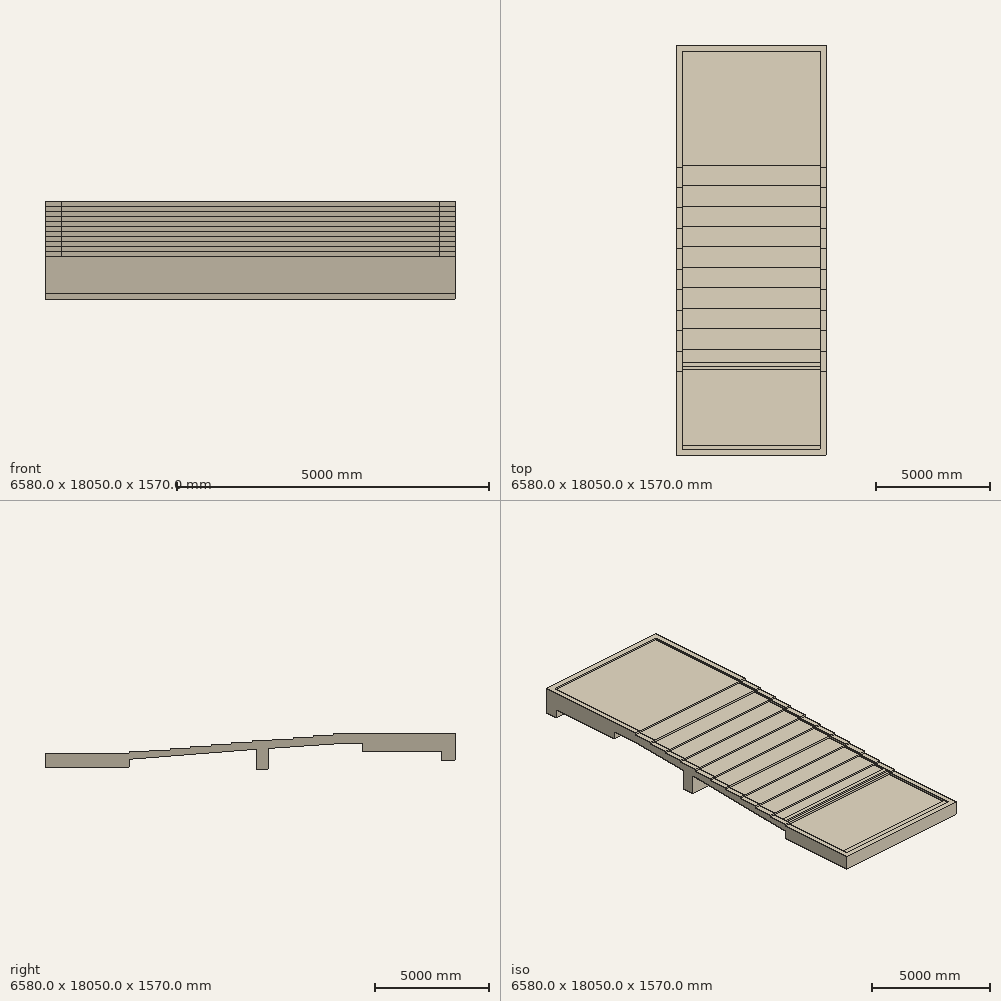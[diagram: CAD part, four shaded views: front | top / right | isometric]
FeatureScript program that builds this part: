
annotation { "Feature Type Name" : "Feature", "Feature Type Description" : "" }
export const myFeature = defineFeature(function(context is Context, id is Id, definition is map)
    precondition{}
    {
        {
            var Q0;
            Q0=qCreatedBy(makeId("Right.planeOp"),FACE);
            var sketch = newSketch(context, id + "F0", { "sketchPlane" : qUnion([Q0])});
            skLineSegment(sketch, "E0", {"start": v(0, 0) * mm, "end": v(-900, 0) * mm});
            skLineSegment(sketch, "E1", {"start": v(-900, 0) * mm, "end": v(-900, -80) * mm});
            skLineSegment(sketch, "E2", {"start": v(-900, -80) * mm, "end": v(-1800, -80) * mm});
            skLineSegment(sketch, "E3", {"start": v(-1800, -80) * mm, "end": v(-1800, -160) * mm});
            skLineSegment(sketch, "E4", {"start": v(-1800, -160) * mm, "end": v(-2700, -160) * mm});
            skLineSegment(sketch, "E5", {"start": v(-2700, -160) * mm, "end": v(-2700, -240) * mm});
            skLineSegment(sketch, "E6", {"start": v(-2700, -240) * mm, "end": v(-3600, -240) * mm});
            skLineSegment(sketch, "E7", {"start": v(-3600, -240) * mm, "end": v(-3600, -320) * mm});
            skLineSegment(sketch, "E8", {"start": v(-3600, -320) * mm, "end": v(-4500, -320) * mm});
            skLineSegment(sketch, "E9", {"start": v(-4500, -320) * mm, "end": v(-4500, -400) * mm});
            skLineSegment(sketch, "E10", {"start": v(-4500, -400) * mm, "end": v(-5400, -400) * mm});
            skLineSegment(sketch, "E11", {"start": v(-5400, -400) * mm, "end": v(-5400, -480) * mm});
            skLineSegment(sketch, "E12", {"start": v(-5400, -480) * mm, "end": v(-6300, -480) * mm});
            skLineSegment(sketch, "E13", {"start": v(-6300, -480) * mm, "end": v(-6300, -560) * mm});
            skLineSegment(sketch, "E14", {"start": v(-6300, -560) * mm, "end": v(-7200, -560) * mm});
            skLineSegment(sketch, "E15", {"start": v(-7200, -560) * mm, "end": v(-7200, -640) * mm});
            skLineSegment(sketch, "E16", {"start": v(-7200, -640) * mm, "end": v(-8100, -640) * mm});
            skLineSegment(sketch, "E17", {"start": v(-8100, -640) * mm, "end": v(-8100, -720) * mm});
            skLineSegment(sketch, "E18", {"start": v(-8100, -720) * mm, "end": v(-9000, -720) * mm});
            skLineSegment(sketch, "E19", {"start": v(-9000, -720) * mm, "end": v(-9000, -800) * mm});
            skLineSegment(sketch, "E20", {"start": v(-9000, -800) * mm, "end": v(-12450, -800) * mm});
            skLineSegment(sketch, "E21", {"start": v(-12450, -800) * mm, "end": v(-12700, -800) * mm});
            skLineSegment(sketch, "E22", {"start": v(-12700, -800) * mm, "end": v(-12700, -800) * mm});
            skLineSegment(sketch, "E23", {"start": v(-12700, -800) * mm, "end": v(-12700, -1300) * mm});
            skLineSegment(sketch, "E24", {"start": v(-12700, -1300) * mm, "end": v(-12700, -1400) * mm});
            skLineSegment(sketch, "E25", {"start": v(-12700, -1400) * mm, "end": v(-9000, -1400) * mm});
            skLineSegment(sketch, "E26", {"start": v(0, 0) * mm, "end": v(0, 80) * mm});
            skLineSegment(sketch, "E27", {"start": v(0, 80) * mm, "end": v(5250, 80) * mm});
            skLineSegment(sketch, "E28", {"start": v(5250, 80) * mm, "end": v(5350, 80) * mm});
            skLineSegment(sketch, "E29", {"start": v(5350, 80) * mm, "end": v(5350, -20) * mm});
            skLineSegment(sketch, "E30", {"start": v(5350, -20) * mm, "end": v(5350, -1020) * mm});
            skLineSegment(sketch, "E31", {"start": v(5350, -1020) * mm, "end": v(5350, -1120) * mm});
            skLineSegment(sketch, "E32", {"start": v(5350, -1120) * mm, "end": v(4750, -1120) * mm});
            skLineSegment(sketch, "E33", {"start": v(4750, -1120) * mm, "end": v(4750, -720) * mm});
            skLineSegment(sketch, "E34", {"start": v(4750, -720) * mm, "end": v(1250, -720) * mm});
            skLineSegment(sketch, "E35", {"start": v(1250, -720) * mm, "end": v(1250, -370) * mm});
            skLineSegment(sketch, "E36", {"start": v(80, 0) * mm, "end": v(80, -80) * mm});
            skLineSegment(sketch, "E37", {"start": v(80, -80) * mm, "end": v(-820, -80) * mm});
            skLineSegment(sketch, "E38", {"start": v(-820, -80) * mm, "end": v(-820, -160) * mm});
            skLineSegment(sketch, "E39", {"start": v(-820, -160) * mm, "end": v(-1720, -160) * mm});
            skLineSegment(sketch, "E40", {"start": v(-1720, -160) * mm, "end": v(-1720, -240) * mm});
            skLineSegment(sketch, "E41", {"start": v(-1720, -240) * mm, "end": v(-2620, -240) * mm});
            skLineSegment(sketch, "E42", {"start": v(-2620, -240) * mm, "end": v(-2620, -320) * mm});
            skLineSegment(sketch, "E43", {"start": v(-2620, -320) * mm, "end": v(-3520, -320) * mm});
            skLineSegment(sketch, "E44", {"start": v(-3520, -320) * mm, "end": v(-3520, -400) * mm});
            skLineSegment(sketch, "E45", {"start": v(-3520, -400) * mm, "end": v(-4420, -400) * mm});
            skLineSegment(sketch, "E46", {"start": v(-4420, -400) * mm, "end": v(-4420, -480) * mm});
            skLineSegment(sketch, "E47", {"start": v(-4420, -480) * mm, "end": v(-5320, -480) * mm});
            skLineSegment(sketch, "E48", {"start": v(-5320, -480) * mm, "end": v(-5320, -560) * mm});
            skLineSegment(sketch, "E49", {"start": v(-5320, -560) * mm, "end": v(-6220, -560) * mm});
            skLineSegment(sketch, "E50", {"start": v(-6220, -560) * mm, "end": v(-6220, -640) * mm});
            skLineSegment(sketch, "E51", {"start": v(-6220, -640) * mm, "end": v(-7120, -640) * mm});
            skLineSegment(sketch, "E52", {"start": v(-7120, -640) * mm, "end": v(-7120, -720) * mm});
            skLineSegment(sketch, "E53", {"start": v(-7120, -720) * mm, "end": v(-8020, -720) * mm});
            skLineSegment(sketch, "E54", {"start": v(-8020, -720) * mm, "end": v(-8020, -800) * mm});
            skLineSegment(sketch, "E55", {"start": v(-8020, -800) * mm, "end": v(-8920, -800) * mm});
            skLineSegment(sketch, "E56", {"start": v(-8920, -800) * mm, "end": v(-8920, -880) * mm});
            skLineSegment(sketch, "E57", {"start": v(-8920, -880) * mm, "end": v(-12450, -880) * mm});
            skLineSegment(sketch, "E58", {"start": v(-12450, -880) * mm, "end": v(-12450, -800) * mm});
            skLineSegment(sketch, "E59.0", {"start": v(-12300, -880) * mm, "end": v(-12300, -800) * mm});
            skLineSegment(sketch, "E60", {"start": v(5250, 80) * mm, "end": v(5100, 80) * mm});
            skLineSegment(sketch, "E61", {"start": v(5100, 80) * mm, "end": v(5100, 0) * mm});
            skLineSegment(sketch, "E62", {"start": v(5100, 0) * mm, "end": v(80, 0) * mm});
            skLineSegment(sketch, "E63", {"start": v(1250, -370) * mm, "end": v(80, -370) * mm});
            skLineSegment(sketch, "E64", {"start": v(-3150, -240) * mm, "end": v(-3150, -320) * mm});
            skLineSegment(sketch, "E65", {"start": v(-3150, -590) * mm, "end": v(-3150, -1390) * mm});
            skLineSegment(sketch, "E66", {"start": v(-3150, -1390) * mm, "end": v(-3150, -1490) * mm});
            skPoint(sketch, "E66.endSnap0", {"position": v(-3150, -990) * mm});
            skLineSegment(sketch, "E67", {"start": v(80, -370) * mm, "end": v(-2875, -571.27) * mm});
            skLineSegment(sketch, "E68", {"start": v(-3150, -1490) * mm, "end": v(-2875, -1490) * mm});
            skLineSegment(sketch, "E69", {"start": v(-2875, -1490) * mm, "end": v(-2875, -571.27) * mm});
            skLineSegment(sketch, "E70.MirrorCS", {"start": v(-3425, -1490) * mm, "end": v(-3425, -571.27) * mm});
            skLineSegment(sketch, "E71", {"start": v(-3150, -1490) * mm, "end": v(-3425, -1490) * mm});
            skLineSegment(sketch, "E72", {"start": v(-9000, -1400) * mm, "end": v(-9000, -1050) * mm});
            skLineSegment(sketch, "E73", {"start": v(-9000, -1050) * mm, "end": v(-3425, -608.73) * mm});
            skSolve(sketch);
        }
        {
            var Q0;
            Q0=makeQuery(id+"F0.imprint","IMPRINT",FACE,{"disambiguationData":[TD([[makeQuery(id+"F0.imprint","IMPRINT",EDGE,{"derivedFrom":sQuery(id+"F0.wireOp",EDGE,"E21")}),1.0]])]});
            extrude(context, id + "F1", {"entities" : qUnion([Q0]), "depth" : 6280 * mm, "offsetDistance" : 25 * mm, "symmetric" : true});
        }
        {
            var Q0;
            {var subQ6=sQuery(id+"F0.wireOp",EDGE,"E7");Q0=makeQuery(id+"F0.imprint","IMPRINT",FACE,{"disambiguationData":[TD([[makeQuery(id+"F0.imprint","IMPRINT",EDGE,{"derivedFrom":subQ6}),1.0]])]});}
            var Q1;
            {var subQ7=sQuery(id+"F0.wireOp",EDGE,"E0");Q1=makeQuery(id+"F0.imprint","IMPRINT",FACE,{"disambiguationData":[TD([[makeQuery(id+"F0.imprint","IMPRINT",EDGE,{"derivedFrom":subQ7}),1.0]])]});}
            var Q2;
            {var subQ0=sQuery(id+"F0.wireOp",EDGE,"E58");Q2=makeQuery(id+"F0.imprint","IMPRINT",FACE,{"disambiguationData":[TD([[makeQuery(id+"F0.imprint","IMPRINT",EDGE,{"derivedFrom":subQ0}),-1.0]])]});}
            var Q3;
            Q3=makeQuery(id+"F0.imprint","IMPRINT",FACE,{"disambiguationData":[TD([[makeQuery(id+"F0.imprint","IMPRINT",EDGE,{"derivedFrom":sQuery(id+"F0.wireOp",EDGE,"E21")}),1.0]])]});
            extrude(context, id + "F2", {"entities" : qUnion([Q0, Q1, Q2, Q3]), "operationType" : NewBodyOperationType.ADD, "depth" : 3290 * mm, "offsetDistance" : 25 * mm, "hasSecondDirection" : true, "secondDirectionOppositeDirection" : false, "secondDirectionDepth" : 3040 * mm});
        }
        {
            var Q0;
            Q0=makeQuery(id+"F0.imprint","IMPRINT",FACE,{"disambiguationData":[TD([[makeQuery(id+"F0.imprint","IMPRINT",EDGE,{"derivedFrom":sQuery(id+"F0.wireOp",EDGE,"E21")}),1.0]])]});
            var Q1;
            Q1=makeQuery(id+"F0.imprint","IMPRINT",FACE,{"disambiguationData":[TD([[makeQuery(id+"F0.imprint","IMPRINT",EDGE,{"derivedFrom":sQuery(id+"F0.wireOp",EDGE,"E0")}),1.0]])]});
            var Q2;
            {var subQ6=sQuery(id+"F0.wireOp",EDGE,"E7");Q2=makeQuery(id+"F0.imprint","IMPRINT",FACE,{"disambiguationData":[TD([[makeQuery(id+"F0.imprint","IMPRINT",EDGE,{"derivedFrom":subQ6}),1.0]])]});}
            var Q3;
            {var subQ0=sQuery(id+"F0.wireOp",EDGE,"E58");Q3=makeQuery(id+"F0.imprint","IMPRINT",FACE,{"disambiguationData":[TD([[makeQuery(id+"F0.imprint","IMPRINT",EDGE,{"derivedFrom":subQ0}),-1.0]])]});}
            extrude(context, id + "F3", {"entities" : qUnion([Q0, Q1, Q2, Q3]), "operationType" : NewBodyOperationType.ADD, "oppositeDirection" : true, "depth" : 3290 * mm, "offsetDistance" : 25 * mm, "hasSecondDirection" : true, "secondDirectionOppositeDirection" : true, "secondDirectionDepth" : 3040 * mm});
        }
        {
            var Q0;
            Q0=qCreatedBy(makeId("Right.planeOp"),FACE);
            var sketch = newSketch(context, id + "F4", { "sketchPlane" : qUnion([Q0])});
            skLineSegment(sketch, "E74", {"start": v(0, 0) * mm, "end": v(-900, 0) * mm});
            skLineSegment(sketch, "E75", {"start": v(-900, 0) * mm, "end": v(-900, -80) * mm});
            skLineSegment(sketch, "E76", {"start": v(-900, -80) * mm, "end": v(-1800, -80) * mm});
            skLineSegment(sketch, "E77", {"start": v(-1800, -80) * mm, "end": v(-1800, -160) * mm});
            skLineSegment(sketch, "E78", {"start": v(-1800, -160) * mm, "end": v(-2700, -160) * mm});
            skLineSegment(sketch, "E79", {"start": v(-2700, -160) * mm, "end": v(-2700, -240) * mm});
            skLineSegment(sketch, "E80", {"start": v(-2700, -240) * mm, "end": v(-3600, -240) * mm});
            skLineSegment(sketch, "E81", {"start": v(-3600, -240) * mm, "end": v(-3600, -320) * mm});
            skLineSegment(sketch, "E82", {"start": v(-3600, -320) * mm, "end": v(-4500, -320) * mm});
            skLineSegment(sketch, "E83", {"start": v(-4500, -320) * mm, "end": v(-4500, -400) * mm});
            skLineSegment(sketch, "E84", {"start": v(-4500, -400) * mm, "end": v(-5400, -400) * mm});
            skLineSegment(sketch, "E85", {"start": v(-5400, -400) * mm, "end": v(-5400, -480) * mm});
            skLineSegment(sketch, "E86", {"start": v(-5400, -480) * mm, "end": v(-6300, -480) * mm});
            skLineSegment(sketch, "E87", {"start": v(-6300, -480) * mm, "end": v(-6300, -560) * mm});
            skLineSegment(sketch, "E88", {"start": v(-6300, -560) * mm, "end": v(-7200, -560) * mm});
            skLineSegment(sketch, "E89", {"start": v(-7200, -560) * mm, "end": v(-7200, -640) * mm});
            skLineSegment(sketch, "E90", {"start": v(-7200, -640) * mm, "end": v(-8100, -640) * mm});
            skLineSegment(sketch, "E91", {"start": v(-8100, -640) * mm, "end": v(-8100, -720) * mm});
            skLineSegment(sketch, "E92", {"start": v(-8100, -720) * mm, "end": v(-9000, -720) * mm});
            skLineSegment(sketch, "E93", {"start": v(-9000, -720) * mm, "end": v(-9000, -800) * mm});
            skLineSegment(sketch, "E94", {"start": v(-9000, -800) * mm, "end": v(-12450, -800) * mm});
            skLineSegment(sketch, "E95", {"start": v(-12450, -800) * mm, "end": v(-12450, -880) * mm});
            skLineSegment(sketch, "E96", {"start": v(-12450, -880) * mm, "end": v(-8920, -880) * mm});
            skLineSegment(sketch, "E97", {"start": v(-8920, -880) * mm, "end": v(-8920, -800) * mm});
            skLineSegment(sketch, "E98", {"start": v(-8920, -800) * mm, "end": v(-8020, -800) * mm});
            skLineSegment(sketch, "E99", {"start": v(-8020, -800) * mm, "end": v(-8020, -720) * mm});
            skLineSegment(sketch, "E100", {"start": v(-8020, -720) * mm, "end": v(-7120, -720) * mm});
            skLineSegment(sketch, "E101", {"start": v(-7120, -720) * mm, "end": v(-7120, -640.41) * mm});
            skLineSegment(sketch, "E102", {"start": v(-7120, -640.41) * mm, "end": v(-6220, -640.41) * mm});
            skLineSegment(sketch, "E103", {"start": v(-6220, -640.41) * mm, "end": v(-6220, -560.41) * mm});
            skLineSegment(sketch, "E104", {"start": v(-6220, -560.41) * mm, "end": v(-5320, -560.41) * mm});
            skLineSegment(sketch, "E105", {"start": v(-5320, -560.41) * mm, "end": v(-5320, -480.41) * mm});
            skLineSegment(sketch, "E106", {"start": v(-5320, -480.41) * mm, "end": v(-4420, -480.41) * mm});
            skLineSegment(sketch, "E107", {"start": v(-4420, -480.41) * mm, "end": v(-4420, -400.41) * mm});
            skLineSegment(sketch, "E108", {"start": v(-4420, -400.41) * mm, "end": v(-3520, -400.41) * mm});
            skLineSegment(sketch, "E109", {"start": v(-3520, -400.41) * mm, "end": v(-3520, -320.41) * mm});
            skLineSegment(sketch, "E110", {"start": v(-3520, -320.41) * mm, "end": v(-2620, -320.41) * mm});
            skLineSegment(sketch, "E111", {"start": v(-2620, -320.41) * mm, "end": v(-2620, -240.41) * mm});
            skLineSegment(sketch, "E112", {"start": v(-2620, -240.41) * mm, "end": v(-1720, -240.41) * mm});
            skLineSegment(sketch, "E113", {"start": v(-1720, -240.41) * mm, "end": v(-1720, -160.41) * mm});
            skLineSegment(sketch, "E114", {"start": v(-1720, -160.41) * mm, "end": v(-820, -160.41) * mm});
            skLineSegment(sketch, "E115", {"start": v(-820, -160.41) * mm, "end": v(-820, -80.41) * mm});
            skLineSegment(sketch, "E116", {"start": v(-820, -80.41) * mm, "end": v(80, -80.41) * mm});
            skLineSegment(sketch, "E117", {"start": v(0, 0) * mm, "end": v(0, 80) * mm});
            skLineSegment(sketch, "E118", {"start": v(0, 80) * mm, "end": v(5250, 80) * mm});
            skLineSegment(sketch, "E119", {"start": v(5250, 80) * mm, "end": v(5100, 80) * mm});
            skLineSegment(sketch, "E120", {"start": v(5100, 80) * mm, "end": v(5100, 0) * mm});
            skLineSegment(sketch, "E121", {"start": v(5100, 0) * mm, "end": v(80, 0) * mm});
            skLineSegment(sketch, "E122", {"start": v(80, 0) * mm, "end": v(80, -80.41) * mm});
            skLineSegment(sketch, "E123", {"start": v(-9000, -800) * mm, "end": v(-8920, -800) * mm});
            skLineSegment(sketch, "E124", {"start": v(-12450, -800) * mm, "end": v(-12253.89, -800) * mm});
            skLineSegment(sketch, "E125", {"start": v(-12253.89, -800) * mm, "end": v(-12253.89, -880) * mm});
            skLineSegment(sketch, "E126.0", {"start": v(-12254.89, -800) * mm, "end": v(-12254.89, -880) * mm});
            skLineSegment(sketch, "E127.0", {"start": v(-12252.89, -800) * mm, "end": v(-12252.89, -880) * mm});
            skLineSegment(sketch, "E128.1.0.0", {"start": v(-12058.78, -800) * mm, "end": v(-12058.78, -880) * mm});
            skLineSegment(sketch, "E128.1.0.1", {"start": v(-12056.78, -800) * mm, "end": v(-12056.78, -880) * mm});
            skLineSegment(sketch, "E128.2.0.0", {"start": v(-11862.67, -800) * mm, "end": v(-11862.67, -880) * mm});
            skLineSegment(sketch, "E128.2.0.1", {"start": v(-11860.67, -800) * mm, "end": v(-11860.67, -880) * mm});
            skLineSegment(sketch, "E128.3.0.0", {"start": v(-11666.56, -800) * mm, "end": v(-11666.56, -880) * mm});
            skLineSegment(sketch, "E128.3.0.1", {"start": v(-11664.56, -800) * mm, "end": v(-11664.56, -880) * mm});
            skLineSegment(sketch, "E128.4.0.0", {"start": v(-11470.44, -800) * mm, "end": v(-11470.44, -880) * mm});
            skLineSegment(sketch, "E128.4.0.1", {"start": v(-11468.44, -800) * mm, "end": v(-11468.44, -880) * mm});
            skLineSegment(sketch, "E128.5.0.0", {"start": v(-11274.33, -800) * mm, "end": v(-11274.33, -880) * mm});
            skLineSegment(sketch, "E128.5.0.1", {"start": v(-11272.33, -800) * mm, "end": v(-11272.33, -880) * mm});
            skLineSegment(sketch, "E128.6.0.0", {"start": v(-11078.22, -800) * mm, "end": v(-11078.22, -880) * mm});
            skLineSegment(sketch, "E128.6.0.1", {"start": v(-11076.22, -800) * mm, "end": v(-11076.22, -880) * mm});
            skLineSegment(sketch, "E128.7.0.0", {"start": v(-10882.11, -800) * mm, "end": v(-10882.11, -880) * mm});
            skLineSegment(sketch, "E128.7.0.1", {"start": v(-10880.11, -800) * mm, "end": v(-10880.11, -880) * mm});
            skLineSegment(sketch, "E128.8.0.0", {"start": v(-10686, -800) * mm, "end": v(-10686, -880) * mm});
            skLineSegment(sketch, "E128.8.0.1", {"start": v(-10684, -800) * mm, "end": v(-10684, -880) * mm});
            skLineSegment(sketch, "E128.9.0.0", {"start": v(-10489.89, -800) * mm, "end": v(-10489.89, -880) * mm});
            skLineSegment(sketch, "E128.9.0.1", {"start": v(-10487.89, -800) * mm, "end": v(-10487.89, -880) * mm});
            skLineSegment(sketch, "E128.10.0.0", {"start": v(-10293.78, -800) * mm, "end": v(-10293.78, -880) * mm});
            skLineSegment(sketch, "E128.10.0.1", {"start": v(-10291.78, -800) * mm, "end": v(-10291.78, -880) * mm});
            skLineSegment(sketch, "E128.11.0.0", {"start": v(-10097.67, -800) * mm, "end": v(-10097.67, -880) * mm});
            skLineSegment(sketch, "E128.11.0.1", {"start": v(-10095.67, -800) * mm, "end": v(-10095.67, -880) * mm});
            skLineSegment(sketch, "E128.12.0.0", {"start": v(-9901.56, -800) * mm, "end": v(-9901.56, -880) * mm});
            skLineSegment(sketch, "E128.12.0.1", {"start": v(-9899.56, -800) * mm, "end": v(-9899.56, -880) * mm});
            skLineSegment(sketch, "E128.13.0.0", {"start": v(-9705.44, -800) * mm, "end": v(-9705.44, -880) * mm});
            skLineSegment(sketch, "E128.13.0.1", {"start": v(-9703.44, -800) * mm, "end": v(-9703.44, -880) * mm});
            skLineSegment(sketch, "E128.14.0.0", {"start": v(-9509.33, -800) * mm, "end": v(-9509.33, -880) * mm});
            skLineSegment(sketch, "E128.14.0.1", {"start": v(-9507.33, -800) * mm, "end": v(-9507.33, -880) * mm});
            skLineSegment(sketch, "E128.15.0.0", {"start": v(-9313.22, -800) * mm, "end": v(-9313.22, -880) * mm});
            skLineSegment(sketch, "E128.15.0.1", {"start": v(-9311.22, -800) * mm, "end": v(-9311.22, -880) * mm});
            skLineSegment(sketch, "E128.16.0.0", {"start": v(-9117.11, -800) * mm, "end": v(-9117.11, -880) * mm});
            skLineSegment(sketch, "E128.16.0.1", {"start": v(-9115.11, -800) * mm, "end": v(-9115.11, -880) * mm});
            skLineSegment(sketch, "E128.direction1", {"start": v(-12254.89, -880) * mm, "end": v(-12058.78, -880) * mm, "construction": true});
            skLineSegment(sketch, "E129", {"start": v(-9000, -720) * mm, "end": v(-8804, -720) * mm});
            skLineSegment(sketch, "E130", {"start": v(-8804, -720) * mm, "end": v(-8805, -720) * mm});
            skLineSegment(sketch, "E131", {"start": v(-8805, -720) * mm, "end": v(-8805, -800) * mm});
            skLineSegment(sketch, "E132", {"start": v(-8804, -720) * mm, "end": v(-8803, -720) * mm});
            skLineSegment(sketch, "E133", {"start": v(-8803, -720) * mm, "end": v(-8803, -800) * mm});
            skLineSegment(sketch, "E134.1.0.0", {"start": v(-8609, -720) * mm, "end": v(-8609, -800) * mm});
            skLineSegment(sketch, "E134.1.0.1", {"start": v(-8607, -720) * mm, "end": v(-8607, -800) * mm});
            skLineSegment(sketch, "E134.2.0.0", {"start": v(-8413, -720) * mm, "end": v(-8413, -800) * mm});
            skLineSegment(sketch, "E134.2.0.1", {"start": v(-8411, -720) * mm, "end": v(-8411, -800) * mm});
            skLineSegment(sketch, "E134.3.0.0", {"start": v(-8217, -720) * mm, "end": v(-8217, -800) * mm});
            skLineSegment(sketch, "E134.3.0.1", {"start": v(-8215, -720) * mm, "end": v(-8215, -800) * mm});
            skLineSegment(sketch, "E134.direction1", {"start": v(-8805, -800) * mm, "end": v(-8609, -800) * mm, "construction": true});
            skLineSegment(sketch, "E135", {"start": v(-8100, -720) * mm, "end": v(-8020, -720) * mm});
            skLineSegment(sketch, "E136", {"start": v(-8100, -640) * mm, "end": v(-7904, -640) * mm});
            skLineSegment(sketch, "E137", {"start": v(-7904, -640) * mm, "end": v(-7905, -640) * mm});
            skLineSegment(sketch, "E138", {"start": v(-7905, -640) * mm, "end": v(-7903, -640) * mm});
            skLineSegment(sketch, "E139", {"start": v(-7903, -640) * mm, "end": v(-7903, -720) * mm});
            skLineSegment(sketch, "E140", {"start": v(-7905, -640) * mm, "end": v(-7905, -720) * mm});
            skLineSegment(sketch, "E141.1.0.0", {"start": v(-7709, -640) * mm, "end": v(-7709, -720) * mm});
            skLineSegment(sketch, "E141.1.0.1", {"start": v(-7707, -640) * mm, "end": v(-7707, -720) * mm});
            skLineSegment(sketch, "E141.2.0.0", {"start": v(-7513, -640) * mm, "end": v(-7513, -720) * mm});
            skLineSegment(sketch, "E141.2.0.1", {"start": v(-7511, -640) * mm, "end": v(-7511, -720) * mm});
            skLineSegment(sketch, "E141.3.0.0", {"start": v(-7317, -640) * mm, "end": v(-7317, -720) * mm});
            skLineSegment(sketch, "E141.3.0.1", {"start": v(-7315, -640) * mm, "end": v(-7315, -720) * mm});
            skLineSegment(sketch, "E141.direction1", {"start": v(-7905, -720) * mm, "end": v(-7709, -720) * mm, "construction": true});
            skLineSegment(sketch, "E142", {"start": v(-7200, -640) * mm, "end": v(-7120, -640.41) * mm});
            skSolve(sketch);
        }
        {
            var Q0;
            {var subQ0=sQuery(id+"F4.wireOp",EDGE,"E95");Q0=makeQuery(id+"F4.imprint","IMPRINT",FACE,{"disambiguationData":[TD([[makeQuery(id+"F4.imprint","IMPRINT",EDGE,{"derivedFrom":subQ0}),1.0]])]});}
            var Q1;
            {var subQ0=sQuery(id+"F4.wireOp",EDGE,"E127.0");Q1=makeQuery(id+"F4.imprint","IMPRINT",FACE,{"disambiguationData":[TD([[makeQuery(id+"F4.imprint","IMPRINT",EDGE,{"derivedFrom":subQ0}),1.0]])]});}
            var Q2;
            {var subQ0=sQuery(id+"F4.wireOp",EDGE,"E128.1.0.1");Q2=makeQuery(id+"F4.imprint","IMPRINT",FACE,{"disambiguationData":[TD([[makeQuery(id+"F4.imprint","IMPRINT",EDGE,{"derivedFrom":subQ0}),1.0]])]});}
            var Q3;
            {var subQ0=sQuery(id+"F4.wireOp",EDGE,"E128.2.0.1");Q3=makeQuery(id+"F4.imprint","IMPRINT",FACE,{"disambiguationData":[TD([[makeQuery(id+"F4.imprint","IMPRINT",EDGE,{"derivedFrom":subQ0}),1.0]])]});}
            var Q4;
            {var subQ0=sQuery(id+"F4.wireOp",EDGE,"E128.3.0.1");Q4=makeQuery(id+"F4.imprint","IMPRINT",FACE,{"disambiguationData":[TD([[makeQuery(id+"F4.imprint","IMPRINT",EDGE,{"derivedFrom":subQ0}),1.0]])]});}
            var Q5;
            {var subQ0=sQuery(id+"F4.wireOp",EDGE,"E128.4.0.1");Q5=makeQuery(id+"F4.imprint","IMPRINT",FACE,{"disambiguationData":[TD([[makeQuery(id+"F4.imprint","IMPRINT",EDGE,{"derivedFrom":subQ0}),1.0]])]});}
            var Q6;
            {var subQ0=sQuery(id+"F4.wireOp",EDGE,"E128.5.0.1");Q6=makeQuery(id+"F4.imprint","IMPRINT",FACE,{"disambiguationData":[TD([[makeQuery(id+"F4.imprint","IMPRINT",EDGE,{"derivedFrom":subQ0}),1.0]])]});}
            var Q7;
            {var subQ0=sQuery(id+"F4.wireOp",EDGE,"E128.6.0.1");Q7=makeQuery(id+"F4.imprint","IMPRINT",FACE,{"disambiguationData":[TD([[makeQuery(id+"F4.imprint","IMPRINT",EDGE,{"derivedFrom":subQ0}),1.0]])]});}
            var Q8;
            {var subQ0=sQuery(id+"F4.wireOp",EDGE,"E128.7.0.1");Q8=makeQuery(id+"F4.imprint","IMPRINT",FACE,{"disambiguationData":[TD([[makeQuery(id+"F4.imprint","IMPRINT",EDGE,{"derivedFrom":subQ0}),1.0]])]});}
            var Q9;
            {var subQ0=sQuery(id+"F4.wireOp",EDGE,"E128.8.0.1");Q9=makeQuery(id+"F4.imprint","IMPRINT",FACE,{"disambiguationData":[TD([[makeQuery(id+"F4.imprint","IMPRINT",EDGE,{"derivedFrom":subQ0}),1.0]])]});}
            var Q10;
            {var subQ0=sQuery(id+"F4.wireOp",EDGE,"E128.9.0.1");Q10=makeQuery(id+"F4.imprint","IMPRINT",FACE,{"disambiguationData":[TD([[makeQuery(id+"F4.imprint","IMPRINT",EDGE,{"derivedFrom":subQ0}),1.0]])]});}
            var Q11;
            {var subQ0=sQuery(id+"F4.wireOp",EDGE,"E128.10.0.1");Q11=makeQuery(id+"F4.imprint","IMPRINT",FACE,{"disambiguationData":[TD([[makeQuery(id+"F4.imprint","IMPRINT",EDGE,{"derivedFrom":subQ0}),1.0]])]});}
            var Q12;
            {var subQ0=sQuery(id+"F4.wireOp",EDGE,"E128.11.0.1");Q12=makeQuery(id+"F4.imprint","IMPRINT",FACE,{"disambiguationData":[TD([[makeQuery(id+"F4.imprint","IMPRINT",EDGE,{"derivedFrom":subQ0}),1.0]])]});}
            var Q13;
            {var subQ0=sQuery(id+"F4.wireOp",EDGE,"E128.12.0.1");Q13=makeQuery(id+"F4.imprint","IMPRINT",FACE,{"disambiguationData":[TD([[makeQuery(id+"F4.imprint","IMPRINT",EDGE,{"derivedFrom":subQ0}),1.0]])]});}
            var Q14;
            {var subQ0=sQuery(id+"F4.wireOp",EDGE,"E128.13.0.1");Q14=makeQuery(id+"F4.imprint","IMPRINT",FACE,{"disambiguationData":[TD([[makeQuery(id+"F4.imprint","IMPRINT",EDGE,{"derivedFrom":subQ0}),1.0]])]});}
            var Q15;
            {var subQ0=sQuery(id+"F4.wireOp",EDGE,"E128.14.0.1");Q15=makeQuery(id+"F4.imprint","IMPRINT",FACE,{"disambiguationData":[TD([[makeQuery(id+"F4.imprint","IMPRINT",EDGE,{"derivedFrom":subQ0}),1.0]])]});}
            var Q16;
            {var subQ0=sQuery(id+"F4.wireOp",EDGE,"E128.15.0.1");Q16=makeQuery(id+"F4.imprint","IMPRINT",FACE,{"disambiguationData":[TD([[makeQuery(id+"F4.imprint","IMPRINT",EDGE,{"derivedFrom":subQ0}),1.0]])]});}
            var Q17;
            {var subQ0=sQuery(id+"F4.wireOp",EDGE,"E128.16.0.1");Q17=makeQuery(id+"F4.imprint","IMPRINT",FACE,{"disambiguationData":[TD([[makeQuery(id+"F4.imprint","IMPRINT",EDGE,{"derivedFrom":subQ0}),1.0]])]});}
            var Q18;
            Q18=makeQuery(id+"F4.imprint","IMPRINT",FACE,{"disambiguationData":[TD([[makeQuery(id+"F4.imprint","IMPRINT",EDGE,{"derivedFrom":sQuery(id+"F4.wireOp",EDGE,"E93")}),1.0]])]});
            var Q19;
            {var subQ0=sQuery(id+"F4.wireOp",EDGE,"E133");Q19=makeQuery(id+"F4.imprint","IMPRINT",FACE,{"disambiguationData":[TD([[makeQuery(id+"F4.imprint","IMPRINT",EDGE,{"derivedFrom":subQ0}),1.0]])]});}
            var Q20;
            {var subQ0=sQuery(id+"F4.wireOp",EDGE,"E134.1.0.1");Q20=makeQuery(id+"F4.imprint","IMPRINT",FACE,{"disambiguationData":[TD([[makeQuery(id+"F4.imprint","IMPRINT",EDGE,{"derivedFrom":subQ0}),1.0]])]});}
            var Q21;
            {var subQ0=sQuery(id+"F4.wireOp",EDGE,"E134.2.0.1");Q21=makeQuery(id+"F4.imprint","IMPRINT",FACE,{"disambiguationData":[TD([[makeQuery(id+"F4.imprint","IMPRINT",EDGE,{"derivedFrom":subQ0}),1.0]])]});}
            var Q22;
            {var subQ0=sQuery(id+"F4.wireOp",EDGE,"E99");Q22=makeQuery(id+"F4.imprint","IMPRINT",FACE,{"disambiguationData":[TD([[makeQuery(id+"F4.imprint","IMPRINT",EDGE,{"derivedFrom":subQ0}),1.0]])]});}
            var Q23;
            Q23=makeQuery(id+"F4.imprint","IMPRINT",FACE,{"disambiguationData":[TD([[makeQuery(id+"F4.imprint","IMPRINT",EDGE,{"derivedFrom":sQuery(id+"F4.wireOp",EDGE,"E91")}),1.0]])]});
            var Q24;
            {var subQ0=sQuery(id+"F4.wireOp",EDGE,"E139");Q24=makeQuery(id+"F4.imprint","IMPRINT",FACE,{"disambiguationData":[TD([[makeQuery(id+"F4.imprint","IMPRINT",EDGE,{"derivedFrom":subQ0}),1.0]])]});}
            var Q25;
            {var subQ0=sQuery(id+"F4.wireOp",EDGE,"E141.1.0.1");Q25=makeQuery(id+"F4.imprint","IMPRINT",FACE,{"disambiguationData":[TD([[makeQuery(id+"F4.imprint","IMPRINT",EDGE,{"derivedFrom":subQ0}),1.0]])]});}
            var Q26;
            {var subQ0=sQuery(id+"F4.wireOp",EDGE,"E141.2.0.1");Q26=makeQuery(id+"F4.imprint","IMPRINT",FACE,{"disambiguationData":[TD([[makeQuery(id+"F4.imprint","IMPRINT",EDGE,{"derivedFrom":subQ0}),1.0]])]});}
            var Q27;
            {var subQ3=sQuery(id+"F4.wireOp",EDGE,"E101");Q27=makeQuery(id+"F4.imprint","IMPRINT",FACE,{"disambiguationData":[TD([[makeQuery(id+"F4.imprint","IMPRINT",EDGE,{"derivedFrom":subQ3}),1.0]])]});}
            extrude(context, id + "F5", {"entities" : qUnion([Q0, Q1, Q2, Q3, Q4, Q5, Q6, Q7, Q8, Q9, Q10, Q11, Q12, Q13, Q14, Q15, Q16, Q17, Q18, Q19, Q20, Q21, Q22, Q23, Q24, Q25, Q26, Q27]), "depth" : 6075 * mm, "offsetDistance" : 25 * mm, "symmetric" : true});
        }
        {
            var Q0;
            Q0=makeQuery(id+"F5.opExtrude","SWEPT_BODY",BODY,{"disambiguationData":[OSD([sQuery(id+"F4.wireOp",EDGE,"E90"),sQuery(id+"F4.wireOp",EDGE,"E100"),sQuery(id+"F4.wireOp",EDGE,"E101"),sQuery(id+"F4.wireOp",EDGE,"E141.3.0.1"),sQuery(id+"F4.wireOp",EDGE,"E142")])]});
            var Q1;
            Q1=makeQuery(id+"F5.opExtrude","SWEPT_BODY",BODY,{"disambiguationData":[OSD([sQuery(id+"F4.wireOp",EDGE,"E90"),sQuery(id+"F4.wireOp",EDGE,"E100"),sQuery(id+"F4.wireOp",EDGE,"E141.1.0.1"),sQuery(id+"F4.wireOp",EDGE,"E141.2.0.0")])]});
            var Q2;
            Q2=makeQuery(id+"F5.opExtrude","SWEPT_BODY",BODY,{"disambiguationData":[OSD([sQuery(id+"F4.wireOp",EDGE,"E90"),sQuery(id+"F4.wireOp",EDGE,"E100"),sQuery(id+"F4.wireOp",EDGE,"E139"),sQuery(id+"F4.wireOp",EDGE,"E141.1.0.0")])]});
            var Q3;
            Q3=makeQuery(id+"F5.opExtrude","SWEPT_BODY",BODY,{"disambiguationData":[OSD([sQuery(id+"F4.wireOp",EDGE,"E91"),sQuery(id+"F4.wireOp",EDGE,"E92"),sQuery(id+"F4.wireOp",EDGE,"E98"),sQuery(id+"F4.wireOp",EDGE,"E99"),sQuery(id+"F4.wireOp",EDGE,"E100"),sQuery(id+"F4.wireOp",EDGE,"E134.3.0.1"),sQuery(id+"F4.wireOp",EDGE,"E136"),sQuery(id+"F4.wireOp",EDGE,"E140")])]});
            var Q4;
            Q4=makeQuery(id+"F5.opExtrude","SWEPT_BODY",BODY,{"disambiguationData":[OSD([sQuery(id+"F4.wireOp",EDGE,"E90"),sQuery(id+"F4.wireOp",EDGE,"E100"),sQuery(id+"F4.wireOp",EDGE,"E141.2.0.1"),sQuery(id+"F4.wireOp",EDGE,"E141.3.0.0")])]});
            var Q5;
            Q5=makeQuery(id+"F5.opExtrude","SWEPT_BODY",BODY,{"disambiguationData":[OSD([sQuery(id+"F4.wireOp",EDGE,"E92"),sQuery(id+"F4.wireOp",EDGE,"E98"),sQuery(id+"F4.wireOp",EDGE,"E134.2.0.1"),sQuery(id+"F4.wireOp",EDGE,"E134.3.0.0")])]});
            var Q6;
            Q6=makeQuery(id+"F5.opExtrude","SWEPT_BODY",BODY,{"disambiguationData":[OSD([sQuery(id+"F4.wireOp",EDGE,"E92"),sQuery(id+"F4.wireOp",EDGE,"E98"),sQuery(id+"F4.wireOp",EDGE,"E134.1.0.1"),sQuery(id+"F4.wireOp",EDGE,"E134.2.0.0")])]});
            var Q7;
            Q7=makeQuery(id+"F5.opExtrude","SWEPT_BODY",BODY,{"disambiguationData":[OSD([sQuery(id+"F4.wireOp",EDGE,"E93"),sQuery(id+"F4.wireOp",EDGE,"E94"),sQuery(id+"F4.wireOp",EDGE,"E96"),sQuery(id+"F4.wireOp",EDGE,"E97"),sQuery(id+"F4.wireOp",EDGE,"E98"),sQuery(id+"F4.wireOp",EDGE,"E128.16.0.1"),sQuery(id+"F4.wireOp",EDGE,"E129"),sQuery(id+"F4.wireOp",EDGE,"E131")])]});
            var Q8;
            Q8=makeQuery(id+"F5.opExtrude","SWEPT_BODY",BODY,{"disambiguationData":[OSD([sQuery(id+"F4.wireOp",EDGE,"E94"),sQuery(id+"F4.wireOp",EDGE,"E96"),sQuery(id+"F4.wireOp",EDGE,"E128.14.0.1"),sQuery(id+"F4.wireOp",EDGE,"E128.15.0.0")])]});
            var Q9;
            Q9=makeQuery(id+"F5.opExtrude","SWEPT_BODY",BODY,{"disambiguationData":[OSD([sQuery(id+"F4.wireOp",EDGE,"E94"),sQuery(id+"F4.wireOp",EDGE,"E96"),sQuery(id+"F4.wireOp",EDGE,"E128.15.0.1"),sQuery(id+"F4.wireOp",EDGE,"E128.16.0.0")])]});
            var Q10;
            Q10=makeQuery(id+"F5.opExtrude","SWEPT_BODY",BODY,{"disambiguationData":[OSD([sQuery(id+"F4.wireOp",EDGE,"E94"),sQuery(id+"F4.wireOp",EDGE,"E96"),sQuery(id+"F4.wireOp",EDGE,"E128.13.0.1"),sQuery(id+"F4.wireOp",EDGE,"E128.14.0.0")])]});
            var Q11;
            Q11=makeQuery(id+"F5.opExtrude","SWEPT_BODY",BODY,{"disambiguationData":[OSD([sQuery(id+"F4.wireOp",EDGE,"E94"),sQuery(id+"F4.wireOp",EDGE,"E96"),sQuery(id+"F4.wireOp",EDGE,"E128.11.0.1"),sQuery(id+"F4.wireOp",EDGE,"E128.12.0.0")])]});
            var Q12;
            Q12=makeQuery(id+"F5.opExtrude","SWEPT_BODY",BODY,{"disambiguationData":[OSD([sQuery(id+"F4.wireOp",EDGE,"E94"),sQuery(id+"F4.wireOp",EDGE,"E96"),sQuery(id+"F4.wireOp",EDGE,"E128.10.0.1"),sQuery(id+"F4.wireOp",EDGE,"E128.11.0.0")])]});
            var Q13;
            Q13=makeQuery(id+"F5.opExtrude","SWEPT_BODY",BODY,{"disambiguationData":[OSD([sQuery(id+"F4.wireOp",EDGE,"E94"),sQuery(id+"F4.wireOp",EDGE,"E96"),sQuery(id+"F4.wireOp",EDGE,"E128.9.0.1"),sQuery(id+"F4.wireOp",EDGE,"E128.10.0.0")])]});
            var Q14;
            Q14=makeQuery(id+"F5.opExtrude","SWEPT_BODY",BODY,{"disambiguationData":[OSD([sQuery(id+"F4.wireOp",EDGE,"E94"),sQuery(id+"F4.wireOp",EDGE,"E96"),sQuery(id+"F4.wireOp",EDGE,"E128.8.0.1"),sQuery(id+"F4.wireOp",EDGE,"E128.9.0.0")])]});
            var Q15;
            Q15=makeQuery(id+"F5.opExtrude","SWEPT_BODY",BODY,{"disambiguationData":[OSD([sQuery(id+"F4.wireOp",EDGE,"E94"),sQuery(id+"F4.wireOp",EDGE,"E96"),sQuery(id+"F4.wireOp",EDGE,"E128.12.0.1"),sQuery(id+"F4.wireOp",EDGE,"E128.13.0.0")])]});
            var Q16;
            Q16=makeQuery(id+"F5.opExtrude","SWEPT_BODY",BODY,{"disambiguationData":[OSD([sQuery(id+"F4.wireOp",EDGE,"E94"),sQuery(id+"F4.wireOp",EDGE,"E96"),sQuery(id+"F4.wireOp",EDGE,"E128.6.0.1"),sQuery(id+"F4.wireOp",EDGE,"E128.7.0.0")])]});
            var Q17;
            Q17=makeQuery(id+"F5.opExtrude","SWEPT_BODY",BODY,{"disambiguationData":[OSD([sQuery(id+"F4.wireOp",EDGE,"E94"),sQuery(id+"F4.wireOp",EDGE,"E96"),sQuery(id+"F4.wireOp",EDGE,"E128.4.0.1"),sQuery(id+"F4.wireOp",EDGE,"E128.5.0.0")])]});
            var Q18;
            Q18=makeQuery(id+"F5.opExtrude","SWEPT_BODY",BODY,{"disambiguationData":[OSD([sQuery(id+"F4.wireOp",EDGE,"E94"),sQuery(id+"F4.wireOp",EDGE,"E96"),sQuery(id+"F4.wireOp",EDGE,"E128.3.0.1"),sQuery(id+"F4.wireOp",EDGE,"E128.4.0.0")])]});
            var Q19;
            Q19=makeQuery(id+"F5.opExtrude","SWEPT_BODY",BODY,{"disambiguationData":[OSD([sQuery(id+"F4.wireOp",EDGE,"E94"),sQuery(id+"F4.wireOp",EDGE,"E96"),sQuery(id+"F4.wireOp",EDGE,"E128.7.0.1"),sQuery(id+"F4.wireOp",EDGE,"E128.8.0.0")])]});
            var Q20;
            Q20=makeQuery(id+"F5.opExtrude","SWEPT_BODY",BODY,{"disambiguationData":[OSD([sQuery(id+"F4.wireOp",EDGE,"E94"),sQuery(id+"F4.wireOp",EDGE,"E96"),sQuery(id+"F4.wireOp",EDGE,"E128.5.0.1"),sQuery(id+"F4.wireOp",EDGE,"E128.6.0.0")])]});
            var Q21;
            Q21=makeQuery(id+"F5.opExtrude","SWEPT_BODY",BODY,{"disambiguationData":[OSD([sQuery(id+"F4.wireOp",EDGE,"E94"),sQuery(id+"F4.wireOp",EDGE,"E96"),sQuery(id+"F4.wireOp",EDGE,"E128.2.0.1"),sQuery(id+"F4.wireOp",EDGE,"E128.3.0.0")])]});
            var Q22;
            Q22=makeQuery(id+"F5.opExtrude","SWEPT_BODY",BODY,{"disambiguationData":[OSD([sQuery(id+"F4.wireOp",EDGE,"E94"),sQuery(id+"F4.wireOp",EDGE,"E96"),sQuery(id+"F4.wireOp",EDGE,"E128.1.0.1"),sQuery(id+"F4.wireOp",EDGE,"E128.2.0.0")])]});
            var Q23;
            Q23=makeQuery(id+"F5.opExtrude","SWEPT_BODY",BODY,{"disambiguationData":[OSD([sQuery(id+"F4.wireOp",EDGE,"E94"),sQuery(id+"F4.wireOp",EDGE,"E96"),sQuery(id+"F4.wireOp",EDGE,"E127.0"),sQuery(id+"F4.wireOp",EDGE,"E128.1.0.0")])]});
            deleteBodies(context, id + "F6", {"entities" : qUnion([Q0, Q1, Q2, Q3, Q4, Q5, Q6, Q7, Q8, Q9, Q10, Q11, Q12, Q13, Q14, Q15, Q16, Q17, Q18, Q19, Q20, Q21, Q22, Q23])});
        }
    });
